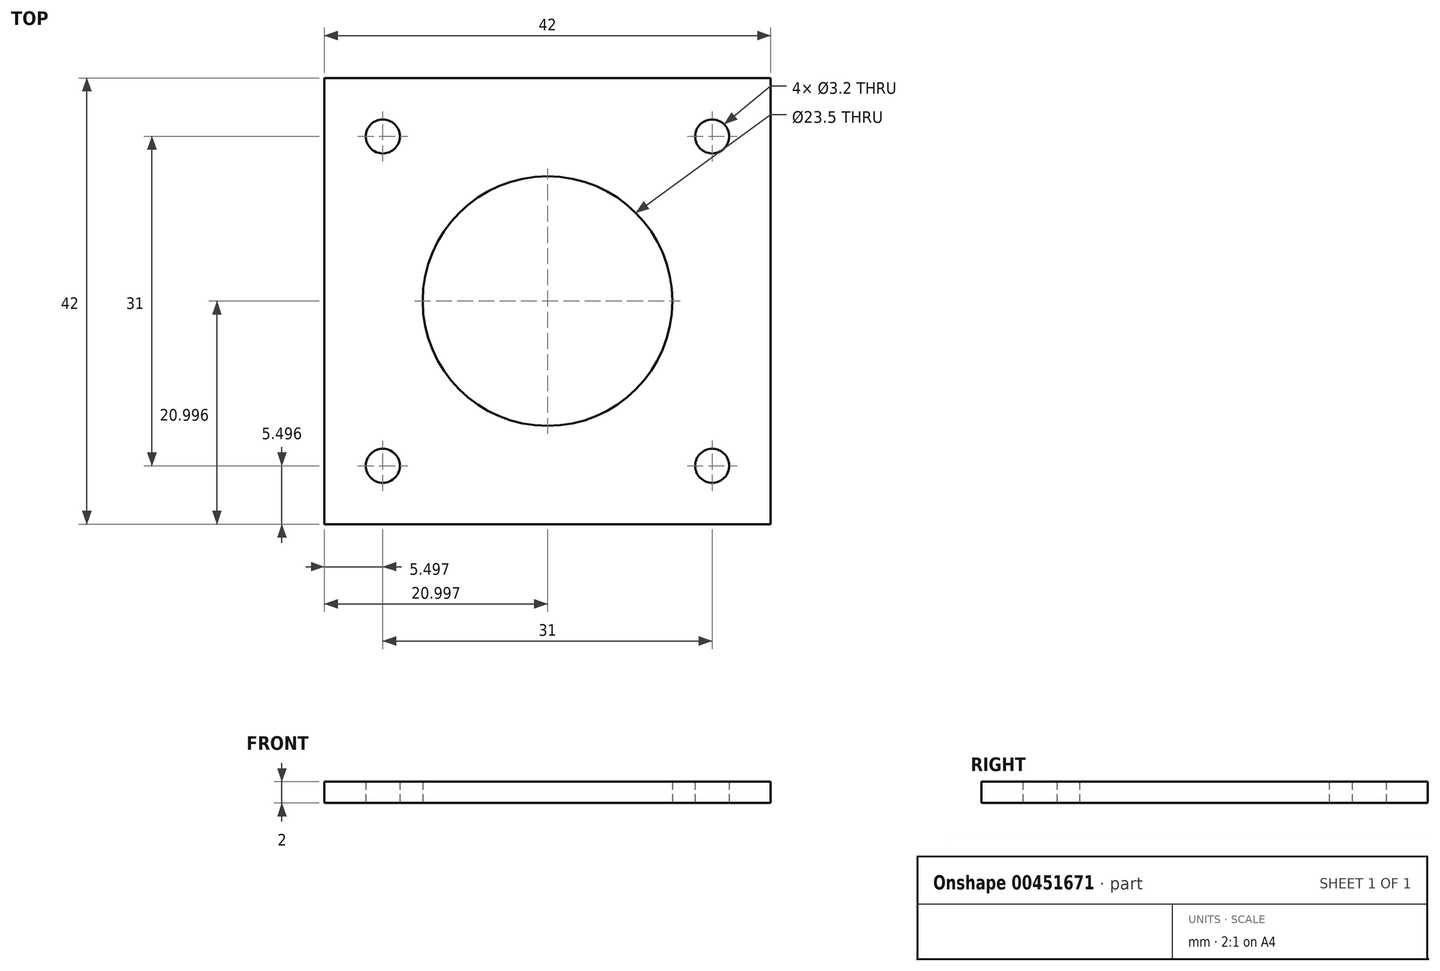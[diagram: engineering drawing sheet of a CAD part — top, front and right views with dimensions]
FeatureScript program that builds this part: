
annotation { "Feature Type Name" : "Feature", "Feature Type Description" : "" }
export const myFeature = defineFeature(function(context is Context, id is Id, definition is map)
    precondition{}
    {
        {
            var Q0;
            Q0=qCreatedBy(makeId("Top.planeOp"),FACE);
            var sketch = newSketch(context, id + "F0", { "sketchPlane" : qUnion([Q0])});
            skLineSegment(sketch, "E0.bottom", {"start": v(-31.98, 24.56) * mm, "end": v(10.02, 24.56) * mm});
            skLineSegment(sketch, "E0.top", {"start": v(-31.98, -17.44) * mm, "end": v(10.02, -17.44) * mm});
            skLineSegment(sketch, "E0.left", {"start": v(-31.98, 24.56) * mm, "end": v(-31.98, -17.44) * mm});
            skLineSegment(sketch, "E0.right", {"start": v(10.02, 24.56) * mm, "end": v(10.02, -17.44) * mm});
            skLineSegment(sketch, "E1", {"start": v(-31.98, 24.56) * mm, "end": v(10.02, -17.44) * mm, "construction": true});
            skCircle(sketch, "E2", {"center": v(-10.98, 3.56) * mm, "radius": 11.75 * mm});
            skLineSegment(sketch, "E3.bottom", {"start": v(-26.48, -11.94) * mm, "end": v(4.52, -11.94) * mm, "construction": true});
            skLineSegment(sketch, "E3.top", {"start": v(-26.48, 19.06) * mm, "end": v(4.52, 19.06) * mm, "construction": true});
            skLineSegment(sketch, "E3.left", {"start": v(-26.48, -11.94) * mm, "end": v(-26.48, 19.06) * mm, "construction": true});
            skLineSegment(sketch, "E3.right", {"start": v(4.52, -11.94) * mm, "end": v(4.52, 19.06) * mm, "construction": true});
            skCircle(sketch, "E4", {"center": v(-26.48, 19.06) * mm, "radius": 1.6 * mm});
            skCircle(sketch, "E5", {"center": v(4.52, 19.06) * mm, "radius": 1.6 * mm});
            skCircle(sketch, "E6", {"center": v(4.52, -11.94) * mm, "radius": 1.6 * mm});
            skCircle(sketch, "E7", {"center": v(-26.48, -11.94) * mm, "radius": 1.6 * mm});
            skSolve(sketch);
        }
        {
            var Q0;
            Q0 = qSketchRegion(id + "F0", true);
            extrude(context, id + "F1", {"entities" : qUnion([Q0]), "depth" : 2 * mm, "offsetDistance" : 25 * mm});
        }
    });
